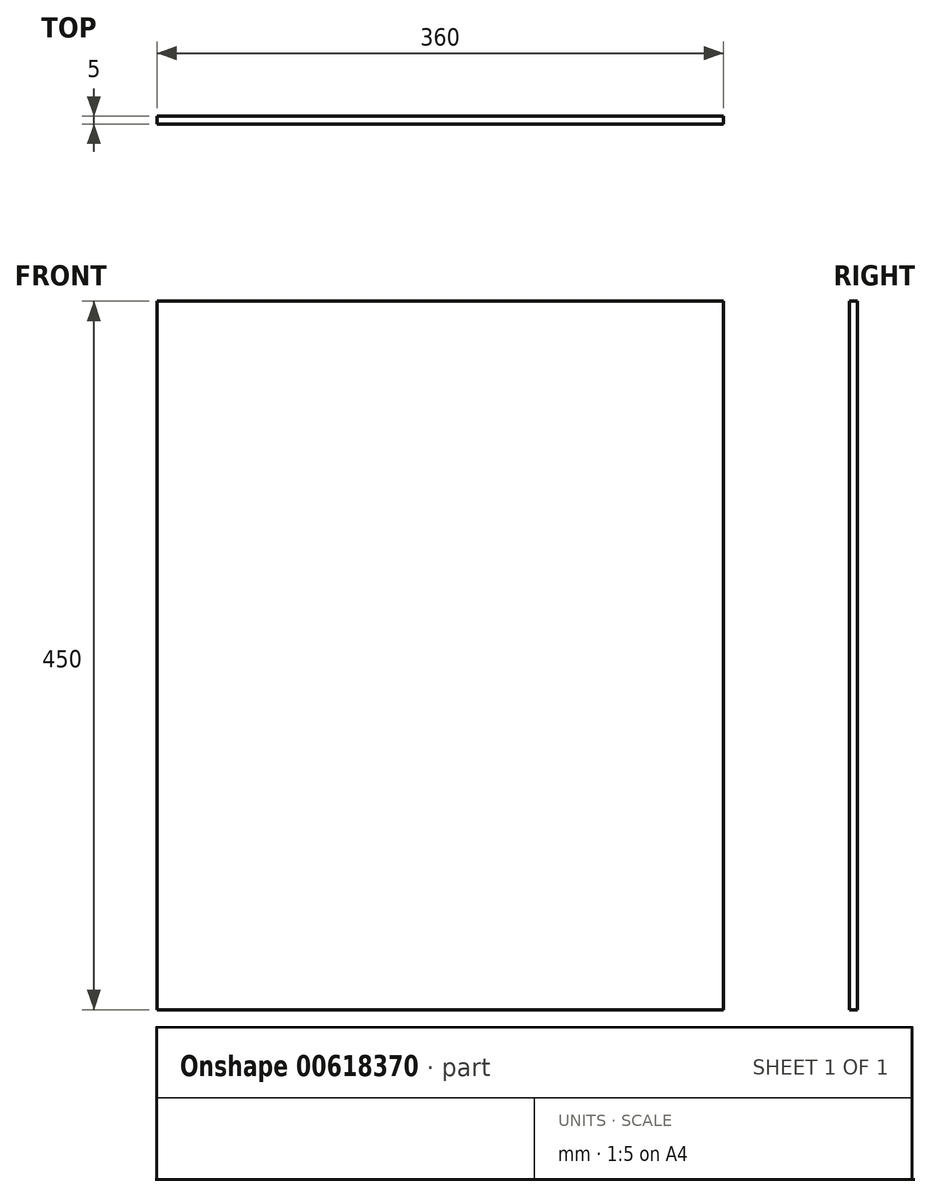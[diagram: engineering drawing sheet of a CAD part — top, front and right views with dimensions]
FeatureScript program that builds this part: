
annotation { "Feature Type Name" : "Feature", "Feature Type Description" : "" }
export const myFeature = defineFeature(function(context is Context, id is Id, definition is map)
    precondition{}
    {
        {
            var Q0;
            Q0=qCreatedBy(makeId("Front.planeOp"),FACE);
            var sketch = newSketch(context, id + "F0", { "sketchPlane" : qUnion([Q0])});
            skLineSegment(sketch, "E0.bottom", {"start": v(180, -225) * mm, "end": v(-180, -225) * mm});
            skLineSegment(sketch, "E0.top", {"start": v(180, 225) * mm, "end": v(-180, 225) * mm});
            skLineSegment(sketch, "E0.left", {"start": v(180, -225) * mm, "end": v(180, 225) * mm});
            skLineSegment(sketch, "E0.right", {"start": v(-180, -225) * mm, "end": v(-180, 225) * mm});
            skPoint(sketch, "E0.middle", {"position": v(0, 0) * mm});
            skSolve(sketch);
        }
        {
            var Q0;
            Q0=makeQuery(id+"F0.imprint","IMPRINT",FACE,{"disambiguationData":[TD([[makeQuery(id+"F0.imprint","IMPRINT",EDGE,{"derivedFrom":sQuery(id+"F0.wireOp",EDGE,"E0.bottom")}),-1.0]])]});
            extrude(context, id + "F1", {"entities" : qUnion([Q0]), "depth" : 2.5 * mm, "offsetDistance" : 25 * mm, "hasSecondDirection" : true, "secondDirectionOppositeDirection" : true, "secondDirectionDepth" : 2.5 * mm});
        }
    });
